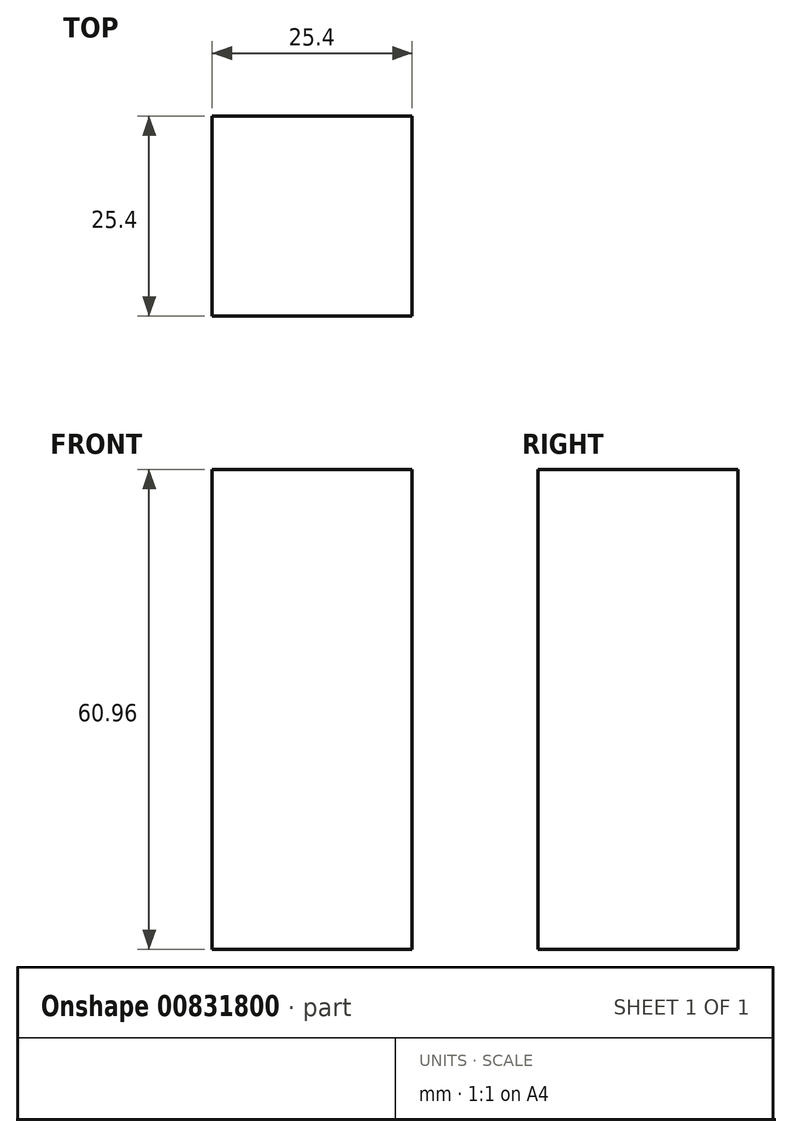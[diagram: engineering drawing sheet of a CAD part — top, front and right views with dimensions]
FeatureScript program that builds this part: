
annotation { "Feature Type Name" : "Feature", "Feature Type Description" : "" }
export const myFeature = defineFeature(function(context is Context, id is Id, definition is map)
    precondition{}
    {
        {
            var Q0;
            Q0=qCreatedBy(makeId("Front.planeOp"),FACE);
            var sketch = newSketch(context, id + "F0", { "sketchPlane" : qUnion([Q0])});
            skLineSegment(sketch, "E0.bottom", {"start": v(-26.94, 18.45) * mm, "end": v(-52.34, 18.45) * mm});
            skLineSegment(sketch, "E0.top", {"start": v(-26.94, -42.51) * mm, "end": v(-52.34, -42.51) * mm});
            skLineSegment(sketch, "E0.left", {"start": v(-26.94, 18.45) * mm, "end": v(-26.94, -42.51) * mm});
            skLineSegment(sketch, "E0.right", {"start": v(-52.34, 18.45) * mm, "end": v(-52.34, -42.51) * mm});
            skSolve(sketch);
        }
        {
            var Q0;
            Q0 = qSketchRegion(id + "F0", true);
            extrude(context, id + "F1", {"entities" : qUnion([Q0]), "depth" : 25.4 * mm, "offsetDistance" : 25.4 * mm});
        }
    });
